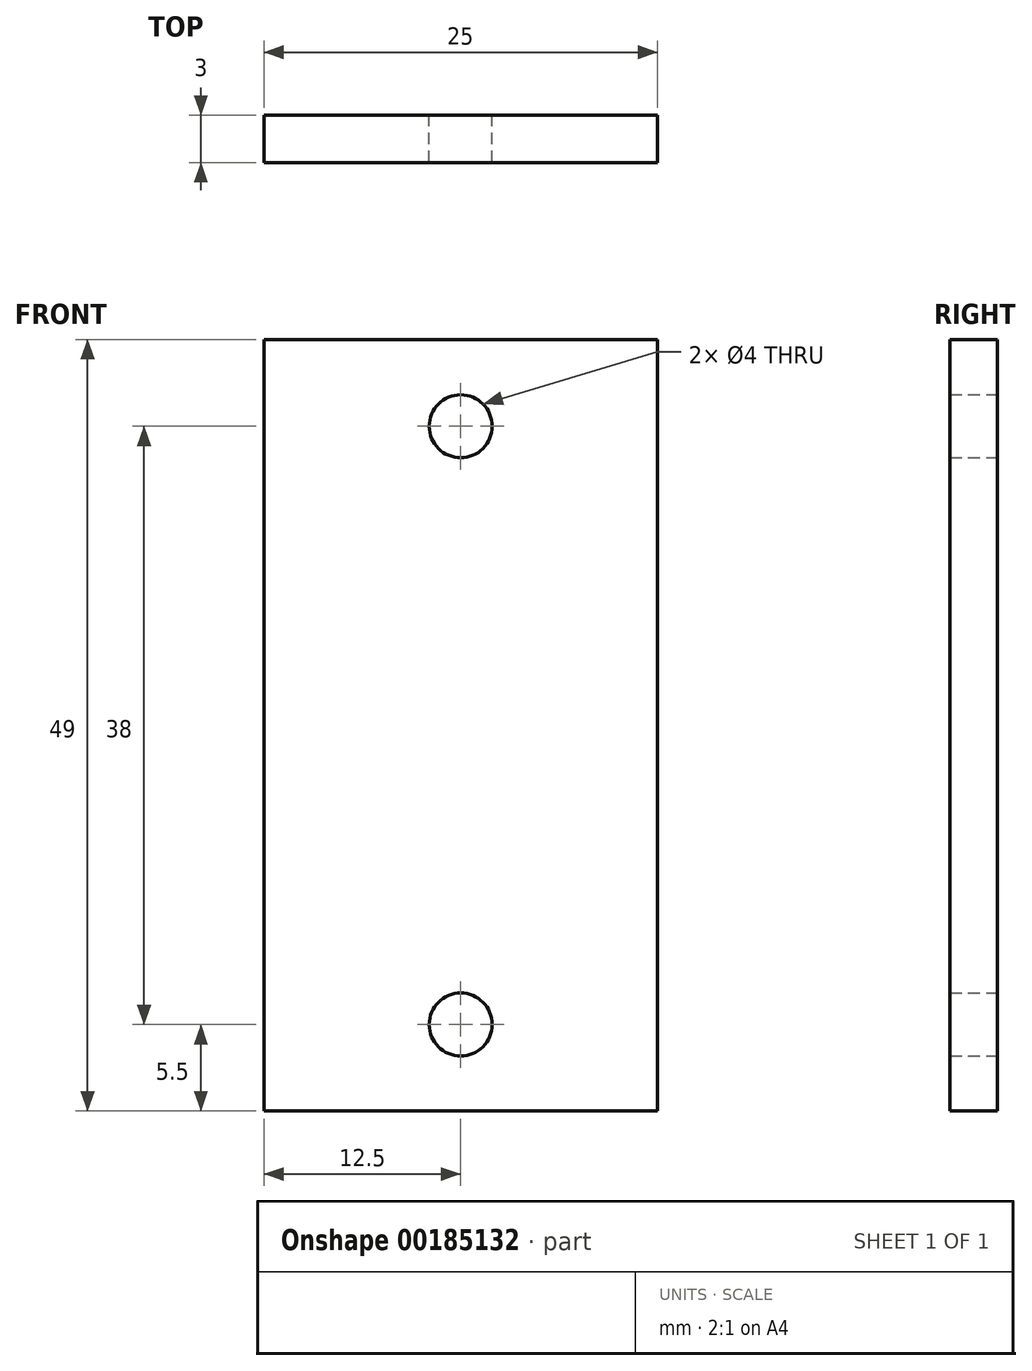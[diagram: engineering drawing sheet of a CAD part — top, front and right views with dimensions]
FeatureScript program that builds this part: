
annotation { "Feature Type Name" : "Feature", "Feature Type Description" : "" }
export const myFeature = defineFeature(function(context is Context, id is Id, definition is map)
    precondition{}
    {
        {
            var Q0;
            Q0=qCreatedBy(makeId("Front.planeOp"),FACE);
            var sketch = newSketch(context, id + "F0", { "sketchPlane" : qUnion([Q0])});
            skLineSegment(sketch, "E0.bottom", {"start": v(-12.5, -24.5) * mm, "end": v(12.5, -24.5) * mm});
            skLineSegment(sketch, "E0.top", {"start": v(-12.5, 24.5) * mm, "end": v(12.5, 24.5) * mm});
            skLineSegment(sketch, "E0.left", {"start": v(-12.5, -24.5) * mm, "end": v(-12.5, 24.5) * mm});
            skLineSegment(sketch, "E0.right", {"start": v(12.5, -24.5) * mm, "end": v(12.5, 24.5) * mm});
            skPoint(sketch, "E0.middle", {"position": v(0, 0) * mm});
            skLineSegment(sketch, "E1", {"start": v(0, 24.5) * mm, "end": v(0, -24.5) * mm, "construction": true});
            skCircle(sketch, "E2", {"center": v(0, 19) * mm, "radius": 2 * mm});
            skLineSegment(sketch, "E3", {"start": v(-12.5, 0) * mm, "end": v(12.5, 0) * mm, "construction": true});
            skCircle(sketch, "E4.MirrorC", {"center": v(0, -19) * mm, "radius": 2 * mm});
            skSolve(sketch);
        }
        {
            var Q0;
            Q0 = qSketchRegion(id + "F0", true);
            extrude(context, id + "F1", {"entities" : qUnion([Q0]), "depth" : 3 * mm});
        }
    });
